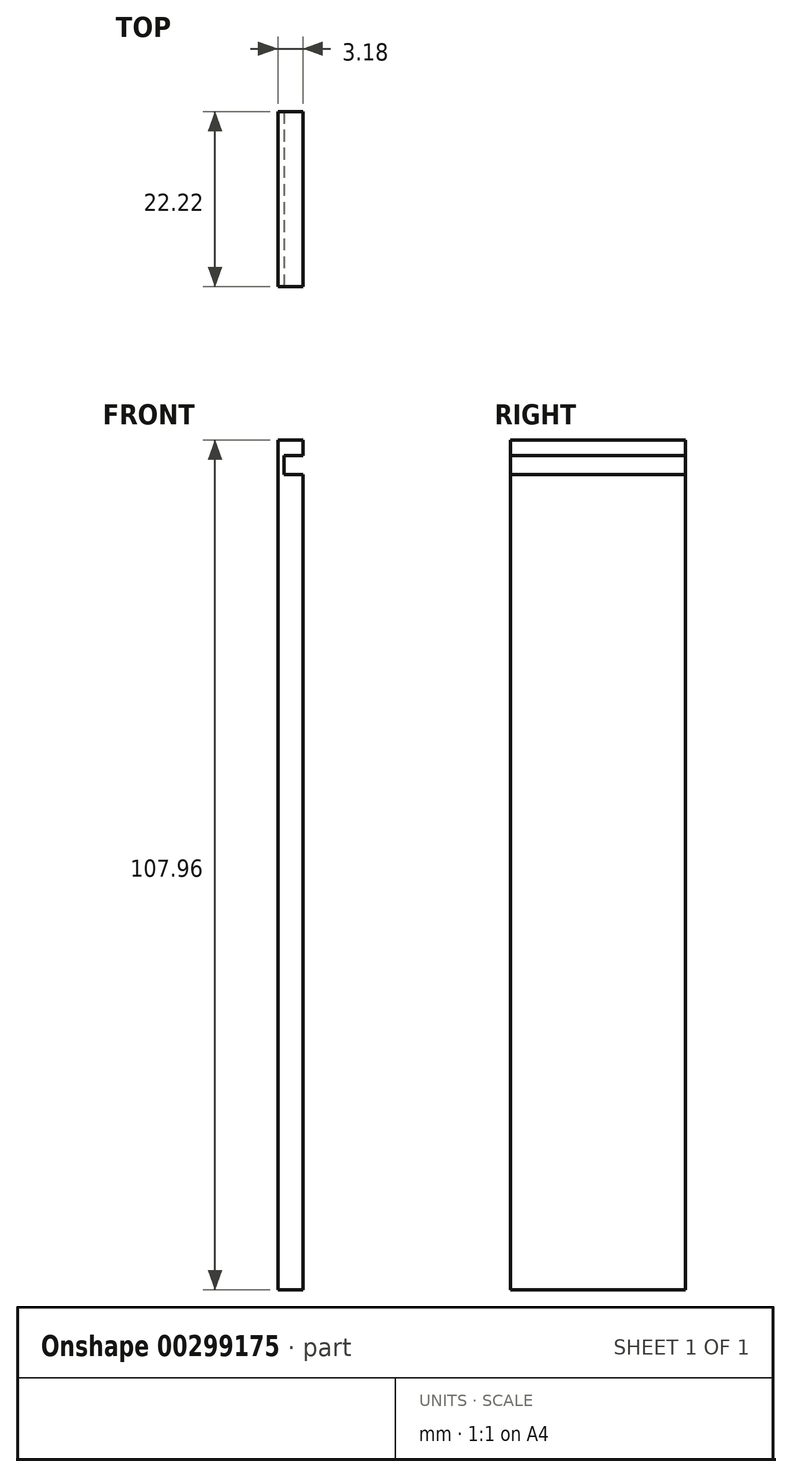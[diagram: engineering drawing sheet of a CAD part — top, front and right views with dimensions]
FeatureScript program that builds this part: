
annotation { "Feature Type Name" : "Feature", "Feature Type Description" : "" }
export const myFeature = defineFeature(function(context is Context, id is Id, definition is map)
    precondition{}
    {
        {
            var Q0;
            Q0=qCreatedBy(makeId("Front.planeOp"),FACE);
            var sketch = newSketch(context, id + "F0", { "sketchPlane" : qUnion([Q0])});
            skLineSegment(sketch, "E0.bottom", {"start": v(1.59, 53.98) * mm, "end": v(-1.59, 53.98) * mm});
            skLineSegment(sketch, "E0.top", {"start": v(1.59, -53.97) * mm, "end": v(-1.59, -53.97) * mm});
            skLineSegment(sketch, "E0.left", {"start": v(1.59, 53.97) * mm, "end": v(1.59, -53.97) * mm});
            skLineSegment(sketch, "E0.right", {"start": v(-1.59, 53.97) * mm, "end": v(-1.59, -53.97) * mm});
            skPoint(sketch, "E0.middle", {"position": v(0, 0) * mm});
            skSolve(sketch);
        }
        {
            var Q0;
            Q0 = qSketchRegion(id + "F0", true);
            extrude(context, id + "F1", {"entities" : qUnion([Q0]), "endBound" : BoundingType.SYMMETRIC, "depth" : 22.22 * mm});
        }
        {
            var Q0;
            Q0=makeQuery(id+"F1.opExtrude","CAP_FACE",FACE,{"disambiguationData":[OSD([sQuery(id+"F0.wireOp",EDGE,"E0.bottom"),sQuery(id+"F0.wireOp",EDGE,"E0.top"),sQuery(id+"F0.wireOp",EDGE,"E0.left"),sQuery(id+"F0.wireOp",EDGE,"E0.right")])],"isStart":false});
            var sketch = newSketch(context, id + "F2", { "sketchPlane" : qUnion([Q0])});
            skLineSegment(sketch, "E1.bottom", {"start": v(1.59, 52) * mm, "end": v(-0.8, 52) * mm});
            skLineSegment(sketch, "E1.top", {"start": v(1.59, 49.6) * mm, "end": v(-0.8, 49.6) * mm});
            skLineSegment(sketch, "E1.left", {"start": v(1.59, 52) * mm, "end": v(1.59, 49.6) * mm});
            skLineSegment(sketch, "E1.right", {"start": v(-0.8, 52) * mm, "end": v(-0.8, 49.6) * mm});
            skSolve(sketch);
        }
        {
            var Q0;
            Q0 = qSketchRegion(id + "F2", true);
            extrude(context, id + "F3", {"entities" : qUnion([Q0]), "operationType" : NewBodyOperationType.REMOVE, "endBound" : BoundingType.THROUGH_ALL, "oppositeDirection" : true, "depth" : 25.4 * mm});
        }
    });
